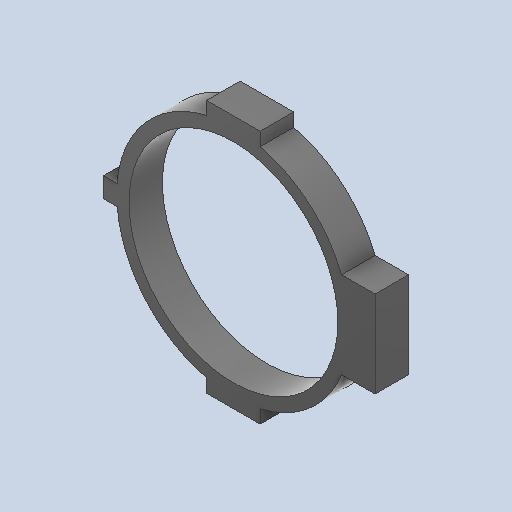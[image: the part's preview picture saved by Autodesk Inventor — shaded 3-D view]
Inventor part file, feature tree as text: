
AUTODESK INVENTOR PART (.ipt)
format: ipt  version: 2022 (Build 260153070, 153G)  size: 142,336 bytes
history: native  units: in
note: dims shown in document units (in); Inventor stores cm internally (conversion verified against a paired STEP export)
features: extrude x1, sketch x1
ambient origin geometry x8: Origin, YZ Plane, XZ Plane, XY Plane, X Axis, Y Axis, Z Axis, Center Point
bodies: Body1 (feature_tree)
feature tree (2):
  extrude  "Extrusion2"  Depth=1.6in
  sketch  "Sketch1"  dims[d2=1.0in d5=0.4in d7=0.4in d8=0.3in d10=1.3in d14=6.25in d15=7.0in d18=1.0in d19=0.0in d24=0.8in d25=0.8in d26=1.6in]
